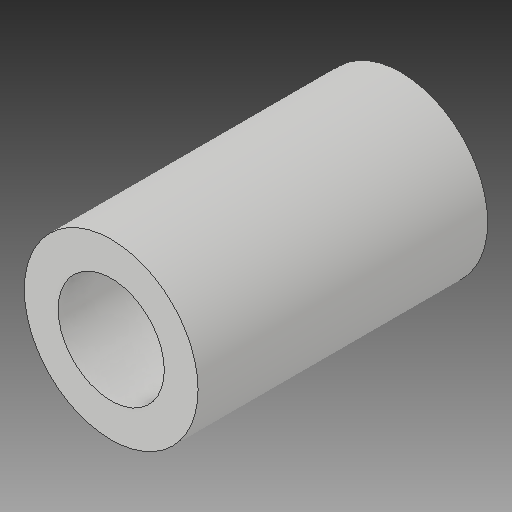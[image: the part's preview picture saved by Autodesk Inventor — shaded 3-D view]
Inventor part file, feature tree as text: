
AUTODESK INVENTOR PART (.ipt)
format: ipt  version: 2017 (Build 210142000, 142)  size: 103,936 bytes
history: native  units: mm
features: other x3, sketch x1
ambient origin geometry x8: Origin, YZ Plane, XZ Plane, XY Plane, X Axis, Y Axis, Z Axis, Center Point
bodies: Solid1 (feature_tree)
feature tree (4):
  other  "Long-Spacer_MIR.ipt"
  other  "Solid1::Long-Spacer_MIR.ipt"
  other  "TaggingFeature1"
  sketch  "Sketch1"  dims[d0=10.0mm]
